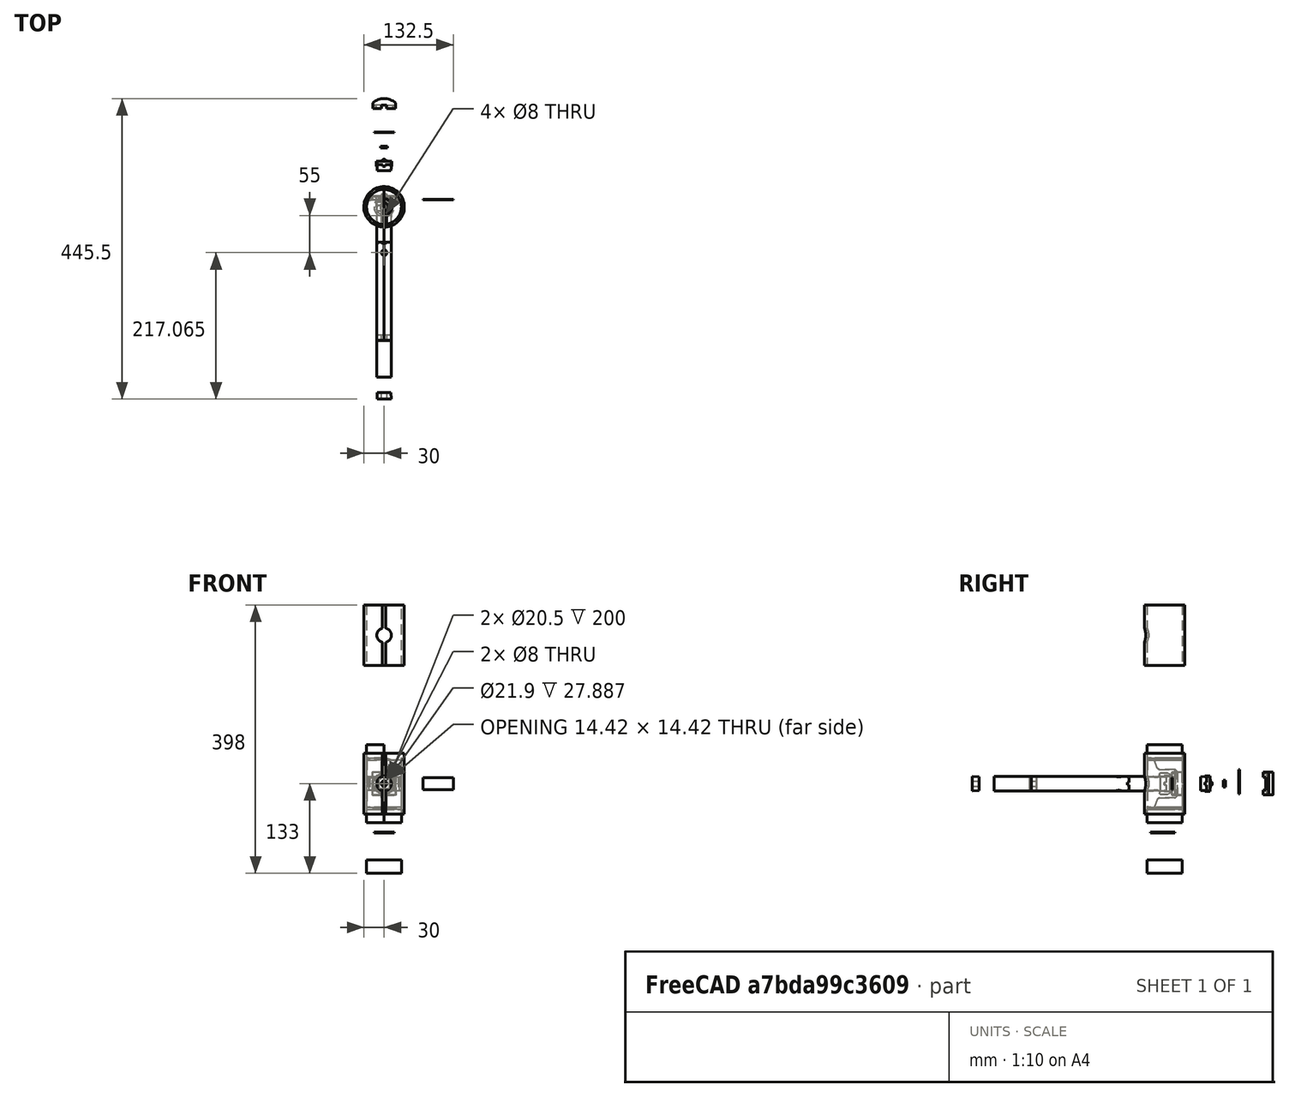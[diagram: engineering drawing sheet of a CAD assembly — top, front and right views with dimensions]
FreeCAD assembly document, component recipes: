
FREECAD ASSEMBLY — COMPONENT RECIPES ("Hammer")

This assembly document has 15 components, labeled P0..P14 below (a component is one placed body or linked part). 15 of them carry a construction recipe — the FreeCAD feature program that regenerates the part from scratch, quoted from this document or its linked companion documents; the rest are supplied as boundary geometry only. No exploded tour is included for this assembly.
NOTE — document 2 of 2 of this assembly tour. The two overview renders and the header above are repeated from document 1; the component sections below continue where the previous document stopped.
COMPONENT P14 — recipe-attached ("PartExploded", modeled in this document).
Construction recipe (the document's own serialized feature program — sketch geometry with constraints, then the solid features built on it; lengths are millimeters unless a unit is written):

FEATURE [Sketcher::SketchObject] Sketch028  label="base001"
  FullyConstrained = true
  MapMode = 5
  Support = -> [XY_Plane016]
  expr: Constraints[1] = <<Properties001>>.Head_ID
  sketch-geometry (1):
    g0: Circle CenterX=0 CenterY=0 CenterZ=0 NormalX=0 NormalY=0 NormalZ=1 AngleXU=0 Radius=25.7
  constraints (2):
    c: Coincident(g0,g-1)
    c: Diameter(g0) = 51.4
FEATURE [PartDesign::Pad] Pad016  label="Base001"
  Direction = (0,0,1)
  Length = 35
  Length2 = 35
  Profile = -> Sketch028
  ReferenceAxis = -> Sketch028 [N_Axis]
  Type = 4
  expr: Length = <<Properties001>>.Insert_Len / 2
  expr: Length2 = <<Properties001>>.Insert_Len / 2
FEATURE [Sketcher::SketchObject] Sketch029  label="sensor_wire_slot001"
  FullyConstrained = true
  MapMode = 5
  Support = -> [XY_Plane016]
  expr: Constraints[11] = <<Properties001>>.Sensor_Wire_Track_Width
  expr: Constraints[1] = Sketch028.Constraints[1]
  sketch-geometry (7):
    g0: Circle CenterX=0 CenterY=0 CenterZ=0 NormalX=0 NormalY=0 NormalZ=1 AngleXU=0 Radius=25.7
    g1: LineSegment StartX=-4 StartY=-25.3868 StartZ=0 EndX=-4 EndY=-14.4568 EndZ=0
    g2: LineSegment StartX=-4 StartY=-14.4568 StartZ=0 EndX=4 EndY=-14.4568 EndZ=0
    g3: LineSegment StartX=4 StartY=-14.4568 StartZ=0 EndX=4 EndY=-25.3868 EndZ=0
    g4: ArcOfCircle CenterX=0 CenterY=0 CenterZ=0 NormalX=0 NormalY=0 NormalZ=1 AngleXU=0 Radius=25.7 StartAngle=4.55611 EndAngle=4.86867
    g5: GeomPoint X=0 Y=-14.4568 Z=0
    g6: Circle CenterX=0 CenterY=0 CenterZ=0 NormalX=0 NormalY=0 NormalZ=1 AngleXU=0 Radius=15
  constraints (17):
    c: Coincident(g0,g-1)
    c: Diameter(g0) = 51.4
    c: Vertical(g1)
    c: Coincident(g2,g1)
    c: Horizontal(g2)
    c: Coincident(g3,g2)
    c: Vertical(g3)
    c: Coincident(g4,g0)
    c: Coincident(g4,g1)
    c: Coincident(g4,g3)
    c: PointOnObject(g3,g0)
    c: DistanceX(g2,g2) = 8
    c: Symmetric(g2,g2,g5)
    c: PointOnObject(g5,g-2)
    c: Coincident(g6,g4)
    c: Diameter(g6) = 30
    c: PointOnObject(g2,g6)
FEATURE [PartDesign::Pocket] Pocket013  label="Sensor_Wire_Slot001"
  BaseFeature = -> Pad016
  Direction = (0,0,-1)
  Length = 35
  Length2 = 35
  Profile = -> Sketch029
  ReferenceAxis = -> Sketch029 [N_Axis]
  Type = 4
  expr: Length = <<Properties001>>.Insert_Len / 2
  expr: Length2 = <<Properties001>>.Insert_Len / 2
FEATURE [Sketcher::SketchObject] Sketch030  label="handle_hole001"
  FullyConstrained = true
  MapMode = 5
  Placement = pos=(0,0,0) rot=(1,0,0;1.5708rad)
  Support = -> [XZ_Plane016]
  expr: Constraints[1] = <<Properties001>>.Handle_OD + <<Properties001>>.Clearance * 2
  sketch-geometry (1):
    g0: Circle CenterX=0 CenterY=0 CenterZ=0 NormalX=0 NormalY=0 NormalZ=1 AngleXU=0 Radius=10.95
  constraints (2):
    c: Coincident(g0,g-1)
    c: Diameter(g0) = 21.9
FEATURE [PartDesign::Pocket] Pocket014  label="Handle_hole001"
  BaseFeature = -> Pocket013
  Direction = (0,1,2e-16)
  Length = 25.7
  Length2 = 25.7
  Profile = -> Sketch030
  ReferenceAxis = -> Sketch030 [N_Axis]
  Type = 4
  expr: Length = <<Properties001>>.Head_ID / 2
  expr: Length2 = <<Properties001>>.Head_ID / 2
FEATURE [Sketcher::SketchObject] Sketch031  label="spring_plate_slot001"
  FullyConstrained = true
  MapMode = 5
  Support = -> [XY_Plane016]
  expr: Constraints[1] = Sketch028.Constraints[1]
  expr: Constraints[3] = <<Properties001>>.Sensor_Diameter + <<Properties001>>.Clearance * 2
  expr: Constraints[7] = <<Properties001>>.Spring_Plate_Len
  sketch-geometry (15):
    g0: Circle CenterX=0 CenterY=0 CenterZ=0 NormalX=0 NormalY=0 NormalZ=1 AngleXU=0 Radius=25.7
    g1: LineSegment StartX=-15.2 StartY=15.4669 StartZ=0 EndX=15.2 EndY=15.4669 EndZ=0
    g2: GeomPoint X=0 Y=15.4669 Z=0
    g3: LineSegment StartX=-23 StartY=11.4669 StartZ=0 EndX=23 EndY=11.4669 EndZ=0
    g4: GeomPoint X=0 Y=11.4669 Z=0
    g5: LineSegment StartX=-15.2 StartY=15.4669 StartZ=0 EndX=-21 EndY=11.4669 EndZ=0
    g6: LineSegment StartX=15.2 StartY=15.4669 StartZ=0 EndX=21 EndY=11.4669 EndZ=0
    g7: LineSegment StartX=21 StartY=11.4669 StartZ=0 EndX=23 EndY=11.4669 EndZ=0
    g8: LineSegment StartX=-21 StartY=11.4669 StartZ=0 EndX=-23 EndY=11.4669 EndZ=0
    g9: ArcOfCircle CenterX=0 CenterY=0 CenterZ=0 NormalX=0 NormalY=0 NormalZ=1 AngleXU=0 Radius=25.7 StartAngle=2.6791 EndAngle=2.80587
    g10: ArcOfCircle CenterX=0 CenterY=0 CenterZ=0 NormalX=0 NormalY=0 NormalZ=1 AngleXU=0 Radius=25.7 StartAngle=0.335723 EndAngle=0.462496
    g11: LineSegment StartX=-11 StartY=10.5 StartZ=0 EndX=-24.2652 EndY=8.46691 EndZ=0
    g12: LineSegment StartX=11 StartY=10.5 StartZ=0 EndX=24.2652 EndY=8.46691 EndZ=0
    g13: LineSegment StartX=11 StartY=10.5 StartZ=0 EndX=-11 EndY=10.5 EndZ=0
    g14: GeomPoint X=0 Y=10.5 Z=0
  constraints (39):
    c: Coincident(g0,g-1)
    c: Diameter(g0) = 51.4
    c: Horizontal(g1)
    c: DistanceX(g1,g1) = 30.4
    c: Symmetric(g1,g1,g2)
    c: PointOnObject(g2,g-2)
    c: Horizontal(g3)
    c: DistanceX(g3,g3) = 46
    c: Symmetric(g3,g3,g4)
    c: PointOnObject(g4,g-2)
    c: Coincident(g5,g1)
    c: PointOnObject(g5,g3)
    c: Coincident(g6,g1)
    c: PointOnObject(g6,g3)
    c: Coincident(g7,g6)
    c: PointOnObject(g7,g0)
    c: Horizontal(g7)
    c: Coincident(g8,g5)
    c: PointOnObject(g8,g0)
    c: Horizontal(g8)
    c: Equal(g8,g7)
    c: PointOnObject(g3,g0)
    c: DistanceY(g6,g1) = 4
    c: DistanceX(g6,g7) = 2
    c: Coincident(g9,g0)
    c: Coincident(g9,g8)
    c: Coincident(g10,g9)
    c: Coincident(g10,g7)
    c: Coincident(g13,g12)
    c: Coincident(g13,g11)
    c: Horizontal(g13)
    c: Coincident(g10,g12)
    c: Coincident(g9,g11)
    c: DistanceX(g12,g6) = 10
    c: Equal(g12,g11)
    c: DistanceY(g10,g7) = 3
    c: Symmetric(g13,g13,g14)
    c: PointOnObject(g14,g-2)
    c: DistanceY(g9,g14) = 10.5
FEATURE [Sketcher::SketchObject] Sketch032  label="top_sensor_hole001"
  FullyConstrained = true
  MapMode = 5
  Placement = pos=(0,0,0) rot=(0.57735,0.57735,0.57735;2.0944rad)
  Support = -> [YZ_Plane016]
  expr: Constraints[20] = <<Properties001>>.Head_ID
  expr: Constraints[7] = <<Properties001>>.Sensor_Diameter + 4
  sketch-geometry (9):
    g0: LineSegment StartX=-25.7 StartY=-17 StartZ=0 EndX=-25.7 EndY=17 EndZ=0
    g1: LineSegment StartX=25.7 StartY=17 StartZ=0 EndX=25.7 EndY=-17 EndZ=0
    g2: LineSegment StartX=25.7 StartY=-17 StartZ=0 EndX=-25.7 EndY=-17 EndZ=0
    g3: GeomPoint X=0 Y=0 Z=0
    g4: LineSegment StartX=10.5 StartY=17 StartZ=0 EndX=25.7 EndY=17 EndZ=0
    g5: LineSegment StartX=25.7 StartY=17 StartZ=0 EndX=25.7 EndY=-17 EndZ=0
    g6: LineSegment StartX=25.7 StartY=-17 StartZ=0 EndX=10.5 EndY=-17 EndZ=0
    g7: LineSegment StartX=10.5 StartY=-17 StartZ=0 EndX=10.5 EndY=17 EndZ=0
    g8: LineSegment StartX=-25.7 StartY=17 StartZ=0 EndX=25.7 EndY=17 EndZ=0
  constraints (23):
    c: Coincident(g1,g2)
    c: Coincident(g2,g0)
    c: Horizontal(g2)
    c: Vertical(g0)
    c: Vertical(g1)
    c: Symmetric(g1,g0,g3)
    c: Coincident(g3,g-1)
    c: DistanceY(g1,g1) = 34
    c: Coincident(g4,g5)
    c: Coincident(g5,g6)
    c: Coincident(g6,g7)
    c: Horizontal(g4)
    c: Horizontal(g6)
    c: Vertical(g5)
    c: Vertical(g7)
    c: PointOnObject(g5,g2)
    c: Coincident(g7,g4)
    c: Coincident(g8,g0)
    c: Coincident(g8,g1)
    c: Horizontal(g8)
    c: DistanceX(g8,g8) = 51.4
    c: Coincident(g4,g1)
    c: DistanceX(g3,g4) = 10.5
FEATURE [PartDesign::Pocket] Pocket015  label="Top_Sensor_Hole001"
  BaseFeature = -> Pocket014
  Direction = (-1,2e-16,-3e-16)
  Length = 17
  Length2 = 17
  Profile = -> Sketch032
  ReferenceAxis = -> Sketch032 [N_Axis]
  Type = 4
  expr: Length = <<Properties001>>.Sensor_Diameter / 2 + 2
  expr: Length2 = <<Properties001>>.Sensor_Diameter / 2 + 2
FEATURE [PartDesign::Chamfer] Chamfer007
  Angle = 70
  Base = -> Pocket015 [Edge30,Edge32]
  BaseFeature = -> Pocket015
  ChamferType = 2
  FlipDirection = false
  Size = 8
  Size2 = 1
  SupportTransform = false
  UseAllEdges = false
FEATURE [PartDesign::Pocket] Pocket016  label="Spring_Plate_Slot001"
  BaseFeature = -> Chamfer007
  Direction = (0,0,-1)
  Length = 10
  Length2 = 10
  Profile = -> Sketch031
  ReferenceAxis = -> Sketch031 [N_Axis]
  Type = 4
FEATURE [PartDesign::Chamfer] Chamfer008
  Angle = 45
  Base = -> Pocket016 [Edge43,Edge46,Edge45,Edge47,Edge44,Edge42]
  BaseFeature = -> Pocket016
  ChamferType = 0
  FlipDirection = false
  Size = 0.5
  Size2 = 1
  SupportTransform = false
  UseAllEdges = false
FEATURE [Sketcher::SketchObject] Sketch033  label="top_sens_base001"
  FullyConstrained = true
  MapMode = 5
  Support = -> [XY_Plane015]
  expr: Constraints[18] = <<Properties001>>.Clearance
  expr: Constraints[1] = <<Properties001>>.Head_ID
  expr: Constraints[3] = 34 - <<Properties001>>.Clearance * 2
  expr: Constraints[6] = 10.5 + <<Properties001>>.Clearance
  sketch-geometry (8):
    g0: Circle CenterX=0 CenterY=0 CenterZ=0 NormalX=0 NormalY=0 NormalZ=1 AngleXU=0 Radius=25.7
    g1: LineSegment StartX=-16.8 StartY=10.7 StartZ=0 EndX=16.8 EndY=10.7 EndZ=0
    g2: GeomPoint X=0 Y=10.7 Z=0
    g3: LineSegment StartX=-16.8 StartY=10.7 StartZ=0 EndX=-16.8 EndY=19.1836 EndZ=0
    g4: LineSegment StartX=16.8 StartY=10.7 StartZ=0 EndX=16.8 EndY=19.1836 EndZ=0
    g5: GeomPoint X=0 Y=25.7 Z=0
    g6: ArcOfCircle CenterX=0 CenterY=0 CenterZ=0 NormalX=0 NormalY=0 NormalZ=1 AngleXU=0 Radius=25.5 StartAngle=0.851542 EndAngle=2.29005
    g7: GeomPoint X=0 Y=25.5 Z=0
  constraints (19):
    c: Coincident(g0,g-1)
    c: Diameter(g0) = 51.4
    c: Horizontal(g1)
    c: DistanceX(g1,g1) = 33.6
    c: Symmetric(g1,g1,g2)
    c: PointOnObject(g2,g-2)
    c: DistanceY(g0,g2) = 10.7
    c: Coincident(g3,g1)
    c: Vertical(g3)
    c: Vertical(g4)
    c: Coincident(g4,g1)
    c: PointOnObject(g5,g0)
    c: PointOnObject(g5,g-2)
    c: Coincident(g6,g0)
    c: Coincident(g6,g3)
    c: Coincident(g6,g4)
    c: PointOnObject(g7,g6)
    c: PointOnObject(g7,g-2)
    c: DistanceY(g7,g5) = 0.2
FEATURE [PartDesign::Pad] Pad017  label="Top_Base001"
  Direction = (0,0,1)
  Length = 16.8
  Length2 = 16.8
  Profile = -> Sketch033
  ReferenceAxis = -> Sketch033 [N_Axis]
  Type = 4
  expr: Length = <<Properties001>>.Sensor_Diameter / 2 + 2 - <<Properties001>>.Clearance
  expr: Length2 = <<Properties001>>.Sensor_Diameter / 2 + 2 - <<Properties001>>.Clearance
FEATURE [Sketcher::SketchObject] Sketch034
  FullyConstrained = true
  MapMode = 5
  Support = -> [XY_Plane015]
  expr: Constraints[1] = Sketch031.Constraints[1]
  expr: Constraints[22] = Sketch031.Constraints[22]
  expr: Constraints[23] = Sketch031.Constraints[23]
  expr: Constraints[33] = Sketch031.Constraints[33]
  expr: Constraints[35] = Sketch031.Constraints[35]
  expr: Constraints[38] = Sketch031.Constraints[38]
  expr: Constraints[3] = Sketch031.Constraints[3]
  expr: Constraints[7] = Sketch031.Constraints[7]
  sketch-geometry (15):
    g0: Circle CenterX=0 CenterY=0 CenterZ=0 NormalX=0 NormalY=0 NormalZ=1 AngleXU=0 Radius=25.7
    g1: LineSegment StartX=-15.2 StartY=15.4669 StartZ=0 EndX=15.2 EndY=15.4669 EndZ=0
    g2: GeomPoint X=0 Y=15.4669 Z=0
    g3: LineSegment StartX=-23 StartY=11.4669 StartZ=0 EndX=23 EndY=11.4669 EndZ=0
    g4: GeomPoint X=0 Y=11.4669 Z=0
    g5: LineSegment StartX=-15.2 StartY=15.4669 StartZ=0 EndX=-21 EndY=11.4669 EndZ=0
    g6: LineSegment StartX=15.2 StartY=15.4669 StartZ=0 EndX=21 EndY=11.4669 EndZ=0
    g7: LineSegment StartX=21 StartY=11.4669 StartZ=0 EndX=23 EndY=11.4669 EndZ=0
    g8: LineSegment StartX=-21 StartY=11.4669 StartZ=0 EndX=-23 EndY=11.4669 EndZ=0
    g9: ArcOfCircle CenterX=0 CenterY=0 CenterZ=0 NormalX=0 NormalY=0 NormalZ=1 AngleXU=0 Radius=25.7 StartAngle=2.6791 EndAngle=2.80587
    g10: ArcOfCircle CenterX=0 CenterY=0 CenterZ=0 NormalX=0 NormalY=0 NormalZ=1 AngleXU=0 Radius=25.7 StartAngle=0.335723 EndAngle=0.462496
    g11: LineSegment StartX=-11 StartY=10.5 StartZ=0 EndX=-24.2652 EndY=8.46691 EndZ=0
    g12: LineSegment StartX=11 StartY=10.5 StartZ=0 EndX=24.2652 EndY=8.46691 EndZ=0
    g13: LineSegment StartX=11 StartY=10.5 StartZ=0 EndX=-11 EndY=10.5 EndZ=0
    g14: GeomPoint X=0 Y=10.5 Z=0
  constraints (40):
    c: Coincident(g0,g-1)
    c: Diameter(g0) = 51.4
    c: Horizontal(g1)
    c: DistanceX(g1,g1) = 30.4
    c: Symmetric(g1,g1,g2)
    c: PointOnObject(g2,g-2)
    c: Horizontal(g3)
    c: DistanceX(g3,g3) = 46
    c: Symmetric(g3,g3,g4)
    c: PointOnObject(g4,g-2)
    c: Coincident(g5,g1)
    c: PointOnObject(g5,g3)
    c: Coincident(g6,g1)
    c: PointOnObject(g6,g3)
    c: Coincident(g7,g6)
    c: PointOnObject(g7,g0)
    c: Horizontal(g7)
    c: Coincident(g8,g5)
    c: PointOnObject(g8,g0)
    c: Horizontal(g8)
    c: Equal(g8,g7)
    c: PointOnObject(g3,g0)
    c: DistanceY(g6,g1) = 4
    c: DistanceX(g6,g7) = 2
    c: Coincident(g9,g0)
    c: Coincident(g9,g8)
    c: Coincident(g10,g9)
    c: Coincident(g10,g7)
    c: Coincident(g13,g12)
    c: Coincident(g13,g11)
    c: Horizontal(g13)
    c: Coincident(g10,g12)
    c: Coincident(g9,g11)
    c: DistanceX(g12,g6) = 10
    c: Equal(g12,g11)
    c: DistanceY(g10,g7) = 3
    c: Symmetric(g13,g13,g14)
    c: PointOnObject(g14,g-2)
    c: DistanceY(g9,g14) = 10.5
    c: DistanceY(g9,g2) = 15.4669
FEATURE [PartDesign::Pocket] Pocket017
  BaseFeature = -> Pad017
  Direction = (0,0,-1)
  Length = 9.5
  Length2 = 9.5
  Profile = -> Sketch034
  ReferenceAxis = -> Sketch034 [N_Axis]
  Type = 4
FEATURE [PartDesign::Chamfer] Chamfer009
  Angle = 45
  Base = -> Pocket017 [Edge22,Edge12]
  BaseFeature = -> Pocket017
  ChamferType = 0
  FlipDirection = false
  Size = 0.3
  Size2 = 1
  SupportTransform = false
  UseAllEdges = false
FEATURE [Sketcher::SketchObject] Sketch035
  FullyConstrained = true
  MapMode = 5
  Placement = pos=(0,0,0) rot=(1,0,0;1.5708rad)
  Support = -> [XZ_Plane015]
  expr: Constraints[11] = <<Properties001>>.Sensor_Wire_Track_Width
  expr: Constraints[1] = <<Properties001>>.Sensor_Diameter + 1
  expr: Constraints[27] = <<Properties001>>.Sensor_Wire_Track_Width
  sketch-geometry (11):
    g0: Circle CenterX=0 CenterY=0 CenterZ=0 NormalX=0 NormalY=0 NormalZ=1 AngleXU=0 Radius=15.5
    g1: LineSegment StartX=-4 StartY=14.975 StartZ=0 EndX=-4 EndY=27.305 EndZ=0
    g2: LineSegment StartX=-4 StartY=27.305 StartZ=0 EndX=4 EndY=27.305 EndZ=0
    g3: LineSegment StartX=4 StartY=27.305 StartZ=0 EndX=4 EndY=14.975 EndZ=0
    g4: GeomPoint X=0 Y=27.305 Z=0
    g5: LineSegment StartX=-4 StartY=-14.975 StartZ=0 EndX=-4 EndY=-27.305 EndZ=0
    g6: LineSegment StartX=-4 StartY=-27.305 StartZ=0 EndX=4 EndY=-27.305 EndZ=0
    g7: LineSegment StartX=4 StartY=-27.305 StartZ=0 EndX=4 EndY=-14.975 EndZ=0
    g8: GeomPoint X=0 Y=-27.305 Z=0
    g9: ArcOfCircle CenterX=0 CenterY=0 CenterZ=0 NormalX=0 NormalY=0 NormalZ=1 AngleXU=0 Radius=15.5 StartAngle=1.83181 EndAngle=4.45137
    g10: ArcOfCircle CenterX=0 CenterY=0 CenterZ=0 NormalX=0 NormalY=0 NormalZ=1 AngleXU=0 Radius=15.5 StartAngle=4.97341 EndAngle=7.59296
  constraints (28):
    c: Coincident(g0,g-1)
    c: Diameter(g0) = 31
    c: PointOnObject(g1,g0)
    c: Vertical(g1)
    c: Coincident(g2,g1)
    c: Horizontal(g2)
    c: Coincident(g3,g2)
    c: PointOnObject(g3,g0)
    c: Vertical(g3)
    c: Symmetric(g2,g2,g4)
    c: PointOnObject(g4,g-2)
    c: DistanceX(g2,g2) = 8
    c: DistanceY(g3,g3) = 12.33
    c: Vertical(g5)
    c: Coincident(g6,g5)
    c: Horizontal(g6)
    c: Coincident(g7,g6)
    c: Vertical(g7)
    c: Symmetric(g6,g6,g8)
    c: PointOnObject(g8,g-2)
    c: Equal(g7,g3)
    c: Coincident(g9,g0)
    c: Coincident(g9,g1)
    c: Coincident(g9,g5)
    c: Coincident(g10,g9)
    c: Coincident(g10,g3)
    c: Coincident(g10,g7)
    c: DistanceX(g6,g6) = 8
FEATURE [PartDesign::Pocket] Pocket018
  BaseFeature = -> Chamfer009
  Direction = (0,1,2e-16)
  Length = 0
  Length2 = 5
  Offset = 0.4
  Profile = -> Sketch035
  ReferenceAxis = -> Sketch035 [N_Axis]
  Type = 3
  UpToFace = -> Chamfer009 [Face11]
FEATURE [PartDesign::Body] Body015  label="TopSensor001"
  Group = -> [Sketch033,Pad017,Sketch034,Pocket017,Chamfer009,Sketch035,Pocket018]
  Origin = -> Origin015
  Placement = pos=(0,135,0) rot=(0,0,1;0rad)
  Tip = -> Pocket018
FEATURE [Sketcher::SketchObject] Sketch036
  FullyConstrained = true
  MapMode = 5
  Placement = pos=(0,0,0) rot=(0.57735,0.57735,0.57735;2.0944rad)
  Support = -> [YZ_Plane016]
  expr: Constraints[16] = <<Properties001>>.Sensor_Diameter + 2
  sketch-geometry (14):
    g0: LineSegment StartX=15.5 StartY=21 StartZ=0 EndX=15.5 EndY=-21 EndZ=0
    g1: LineSegment StartX=15.5 StartY=-21 StartZ=0 EndX=-19.02 EndY=-21 EndZ=0
    g2: LineSegment StartX=-19.02 StartY=-21 StartZ=0 EndX=-19.02 EndY=-16 EndZ=0
    g3: LineSegment StartX=-19.02 StartY=-16 StartZ=0 EndX=10.5 EndY=-16 EndZ=0
    g4: LineSegment StartX=10.5 StartY=-16 StartZ=0 EndX=10.5 EndY=16 EndZ=0
    g5: LineSegment StartX=10.5 StartY=16 StartZ=0 EndX=-19.02 EndY=16 EndZ=0
    g6: LineSegment StartX=-19.02 StartY=16 StartZ=0 EndX=-19.02 EndY=21 EndZ=0
    g7: LineSegment StartX=-19.02 StartY=21 StartZ=0 EndX=15.5 EndY=21 EndZ=0
    g8: GeomPoint X=10.5 Y=0 Z=0
    g9: GeomPoint X=15.5 Y=0 Z=0
    g10: GeomPoint X=15.5 Y=21 Z=0
    g11: GeomPoint X=15.5 Y=-21 Z=0
    g12: GeomPoint X=10.5 Y=16 Z=0
    g13: GeomPoint X=10.5 Y=-16 Z=0
  constraints (30):
    c: Vertical(g0)
    c: Horizontal(g1)
    c: Coincident(g2,g1)
    c: Vertical(g2)
    c: Coincident(g3,g2)
    c: Horizontal(g3)
    c: Vertical(g4)
    c: Horizontal(g5)
    c: Coincident(g6,g5)
    c: Vertical(g6)
    c: Coincident(g7,g6)
    c: Horizontal(g7)
    c: Symmetric(g10,g11,g9)
    c: Symmetric(g13,g12,g8)
    c: PointOnObject(g8,g-1)
    c: PointOnObject(g9,g-1)
    c: DistanceY(g13,g12) = 32
    c: DistanceY(g6,g6) = 5
    c: DistanceX(g8,g9) = 5
    c: DistanceX(g-1,g8) = 10.5
    c: DistanceX(g7,g10) = 34.52
    c: Coincident(g0,g10)
    c: Coincident(g7,g0)
    c: Coincident(g4,g12)
    c: Coincident(g5,g4)
    c: Coincident(g0,g11)
    c: Coincident(g4,g13)
    c: Coincident(g3,g4)
    c: Coincident(g1,g0)
    c: Equal(g3,g5)
FEATURE [PartDesign::Pocket] Pocket019
  BaseFeature = -> Chamfer008
  Direction = (-1,2e-16,-3e-16)
  Length = 4
  Length2 = 4
  Profile = -> Sketch036
  ReferenceAxis = -> Sketch036 [N_Axis]
  Type = 4
  expr: Length = <<Properties001>>.Sensor_Wire_Track_Width / 2
  expr: Length2 = <<Properties001>>.Sensor_Wire_Track_Width / 2
FEATURE [PartDesign::Chamfer] Chamfer010
  Angle = 65
  Base = -> Pocket019 [Edge148,Edge154]
  BaseFeature = -> Pocket019
  ChamferType = 2
  FlipDirection = false
  Size = 3
  Size2 = 1
  SupportTransform = false
  UseAllEdges = false
FEATURE [PartDesign::Chamfer] Chamfer011
  Angle = 45
  Base = -> Chamfer010 [Edge167,Edge85,Edge52,Edge56]
  BaseFeature = -> Chamfer010
  ChamferType = 0
  FlipDirection = false
  Size = 2
  Size2 = 1
  SupportTransform = false
  UseAllEdges = false
FEATURE [PartDesign::Chamfer] Chamfer012
  Angle = 45
  Base = -> Chamfer011 [Edge169,Edge38]
  BaseFeature = -> Chamfer011
  ChamferType = 1
  FlipDirection = false
  Size = 4
  Size2 = 3.999
  SupportTransform = false
  UseAllEdges = false
FEATURE [PartDesign::AdditiveCone] Cone002
  Angle = 360
  AttacherType = Attacher::AttachEngine3D
  BaseFeature = -> Chamfer012
  Height = 1.5
  MapMode = 5
  Placement = pos=(0,0,35) rot=(0,0,1;0rad)
  Radius1 = 12
  Radius2 = 6
  Support = -> [Chamfer012]
FEATURE [PartDesign::AdditiveCone] Cone003
  Angle = 360
  AttacherType = Attacher::AttachEngine3D
  BaseFeature = -> Cone002
  Height = 1.5
  MapMode = 5
  Placement = pos=(0,0,-35) rot=(1,0,0;3.14159rad)
  Radius1 = 12
  Radius2 = 6
  Support = -> [Cone002]
FEATURE [Sketcher::SketchObject] Sketch037
  FullyConstrained = true
  MapMode = 5
  Support = -> [XY_Plane017]
  sketch-geometry (2):
    g0: Circle CenterX=0 CenterY=0 CenterZ=0 NormalX=0 NormalY=0 NormalZ=1 AngleXU=0 Radius=26
    g1: Circle CenterX=0 CenterY=0 CenterZ=0 NormalX=0 NormalY=0 NormalZ=1 AngleXU=0 Radius=30
  constraints (4):
    c: Coincident(g0,g-1)
    c: Coincident(g1,g0)
    c: Diameter(g0) = 52
    c: Diameter(g1) = 60
FEATURE [PartDesign::Pad] Pad018
  Direction = (0,0,1)
  Length = 45
  Length2 = 45
  Profile = -> Sketch037
  ReferenceAxis = -> Sketch037 [N_Axis]
  Type = 4
FEATURE [Sketcher::SketchObject] Sketch038
  FullyConstrained = true
  MapMode = 5
  Placement = pos=(0,0,0) rot=(1,0,0;1.5708rad)
  Support = -> [XZ_Plane017]
  expr: Constraints[1] = <<Properties001>>.Handle_OD
  sketch-geometry (1):
    g0: Circle CenterX=0 CenterY=0 CenterZ=0 NormalX=0 NormalY=0 NormalZ=1 AngleXU=0 Radius=10.75
  constraints (2):
    c: Coincident(g0,g-1)
    c: Diameter(g0) = 21.5
FEATURE [PartDesign::Pocket] Pocket020
  BaseFeature = -> Pad018
  Direction = (0,1,2e-16)
  Length = 5
  Length2 = 5
  Profile = -> Sketch038
  ReferenceAxis = -> Sketch038 [N_Axis]
  Reversed = true
  Type = 1
FEATURE [Sketcher::SketchObject] Sketch039
  FullyConstrained = true
  MapMode = 5
  Placement = pos=(0,0,0) rot=(1,0,0;1.5708rad)
  Support = -> [XZ_Plane018]
  expr: Constraints[3] = <<Properties001>>.Handle_ID
  sketch-geometry (2):
    g0: Circle CenterX=0 CenterY=0 CenterZ=0 NormalX=0 NormalY=0 NormalZ=1 AngleXU=0 Radius=10.625
    g1: Circle CenterX=0 CenterY=0 CenterZ=0 NormalX=0 NormalY=0 NormalZ=1 AngleXU=0 Radius=10.25
  constraints (4):
    c: Coincident(g0,g-1)
    c: Diameter(g0) = 21.25
    c: Coincident(g1,g0)
    c: Diameter(g1) = 20.5
FEATURE [PartDesign::Pad] Pad019
  Direction = (0,-1,-2e-16)
  Length = 200
  Length2 = 10
  Placement = pos=(0,0,0) rot=(1,0,0;1.5708rad)
  Profile = -> Sketch039
  ReferenceAxis = -> Sketch039 [N_Axis]
  Type = 0
FEATURE [Sketcher::SketchObject] Sketch040
  FullyConstrained = true
  MapMode = 5
  Support = -> [XY_Plane019]
  sketch-geometry (5):
    g0: ArcOfCircle CenterX=0 CenterY=0 CenterZ=0 NormalX=0 NormalY=0 NormalZ=1 AngleXU=0 Radius=15 StartAngle=4.90695 EndAngle=10.801
    g1: LineSegment StartX=2.9 StartY=-14.717 StartZ=0 EndX=2.9 EndY=-20.717 EndZ=0
    g2: LineSegment StartX=2.9 StartY=-20.717 StartZ=0 EndX=-2.9 EndY=-20.717 EndZ=0
    g3: LineSegment StartX=-2.9 StartY=-20.717 StartZ=0 EndX=-2.9 EndY=-14.717 EndZ=0
    g4: LineSegment StartX=2.9 StartY=-14.717 StartZ=0 EndX=-2.9 EndY=-14.717 EndZ=0
  constraints (14):
    c: Coincident(g0,g-1)
    c: Radius(g0) = 15
    c: Coincident(g1,g0)
    c: Vertical(g1)
    c: Coincident(g2,g1)
    c: Horizontal(g2)
    c: Coincident(g3,g2)
    c: Coincident(g3,g0)
    c: Vertical(g3)
    c: DistanceX(g2,g2) = 5.8
    c: Coincident(g4,g0)
    c: Coincident(g4,g0)
    c: Horizontal(g4)
    c: DistanceY(g1,g1) = 6
FEATURE [PartDesign::Pad] Pad020
  Direction = (0,0,1)
  Length = 1
  Length2 = 10
  Profile = -> Sketch040
  ReferenceAxis = -> Sketch040 [N_Axis]
  Type = 0
FEATURE [PartDesign::Body] Body018  label="Sensor004"
  Group = -> [Sketch040,Pad020]
  Origin = -> Origin019
  Placement = pos=(0,0,72) rot=(0,0,1;0rad)
  Tip = -> Pad020
FEATURE [PartDesign::FeatureBase] Clone003
  BaseFeature = -> Body018
FEATURE [PartDesign::Body] Body019  label="Sensor005"
  Group = -> [Clone003]
  Origin = -> Origin020
  Placement = pos=(0,0,-72) rot=(0,1,0;3.14159rad)
  Tip = -> Clone003
FEATURE [PartDesign::FeatureBase] Clone004
  BaseFeature = -> Body018
FEATURE [PartDesign::Body] Body020  label="Sensor006"
  Group = -> [Clone004]
  Origin = -> Origin021
  Placement = pos=(0,111,1.7e-14) rot=(0,0.707107,-0.707107;3.14159rad)
  Tip = -> Clone004
FEATURE [Sketcher::SketchObject] Sketch041
  FullyConstrained = true
  MapMode = 5
  Support = -> [XY_Plane022]
  sketch-geometry (1):
    g0: Circle CenterX=0 CenterY=0 CenterZ=0 NormalX=0 NormalY=0 NormalZ=1 AngleXU=0 Radius=26
  constraints (2):
    c: Coincident(g0,g-1)
    c: Diameter(g0) = 52
FEATURE [PartDesign::Pad] Pad021
  Direction = (0,0,1)
  Length = 20
  Length2 = 10
  Profile = -> Sketch041
  ReferenceAxis = -> Sketch041 [N_Axis]
  Type = 0
FEATURE [PartDesign::Body] Body021  label="Foam003"
  Group = -> [Sketch041,Pad021]
  Origin = -> Origin022
  Placement = pos=(0,0,108) rot=(0,0,1;0rad)
  Tip = -> Pad021
FEATURE [PartDesign::FeatureBase] Clone005
  BaseFeature = -> Body021
  Placement = pos=(0,0,38) rot=(0,0,1;0rad)
FEATURE [PartDesign::Body] Body022  label="Foam004"
  Group = -> [Clone005]
  Origin = -> Origin023
  Placement = pos=(0,0,-75) rot=(1,0,0;3.14159rad)
  Tip = -> Clone005
FEATURE [Sketcher::SketchObject] Sketch042
  FullyConstrained = true
  MapMode = 5
  Support = -> [XY_Plane024]
  sketch-geometry (5):
    g0: LineSegment StartX=-22.5 StartY=-0.4 StartZ=0 EndX=-22.5 EndY=0.4 EndZ=0
    g1: LineSegment StartX=-22.5 StartY=0.4 StartZ=0 EndX=22.5 EndY=0.4 EndZ=0
    g2: LineSegment StartX=22.5 StartY=0.4 StartZ=0 EndX=22.5 EndY=-0.4 EndZ=0
    g3: LineSegment StartX=22.5 StartY=-0.4 StartZ=0 EndX=-22.5 EndY=-0.4 EndZ=0
    g4: GeomPoint X=0 Y=0 Z=0
  constraints (12):
    c: Coincident(g0,g1)
    c: Coincident(g1,g2)
    c: Coincident(g2,g3)
    c: Coincident(g3,g0)
    c: Horizontal(g1)
    c: Horizontal(g3)
    c: Vertical(g0)
    c: Vertical(g2)
    c: Symmetric(g1,g0,g4)
    c: Coincident(g4,g-1)
    c: DistanceX(g1,g1) = 45
    c: DistanceY(g2,g2) = 0.8
FEATURE [PartDesign::Pad] Pad022
  Direction = (0,0,1)
  Length = 9
  Length2 = 9
  Profile = -> Sketch042
  ReferenceAxis = -> Sketch042 [N_Axis]
  Type = 4
FEATURE [PartDesign::Body] Body023  label="ShimStock001"
  Group = -> [Sketch042,Pad022]
  Origin = -> Origin024
  Placement = pos=(80,11,0) rot=(0,0,1;0rad)
  Tip = -> Pad022
FEATURE [Sketcher::SketchObject] Sketch043
  FullyConstrained = true
  MapMode = 5
  Placement = pos=(0,0,0) rot=(1,0,0;1.5708rad)
  Support = -> [XZ_Plane025]
  sketch-geometry (1):
    g0: Circle CenterX=0 CenterY=0 CenterZ=0 NormalX=0 NormalY=0 NormalZ=1 AngleXU=0 Radius=5
  constraints (2):
    c: Coincident(g0,g-1)
    c: Diameter(g0) = 10
FEATURE [PartDesign::Pad] Pad023
  Direction = (0,-1,-2e-16)
  Length = 3
  Length2 = 10
  Placement = pos=(0,0,0) rot=(1,0,0;1.5708rad)
  Profile = -> Sketch043
  ReferenceAxis = -> Sketch043 [N_Axis]
  Type = 0
FEATURE [PartDesign::Body] Body024  label="TopFoam001"
  Group = -> [Sketch043,Pad023]
  Origin = -> Origin025
  Placement = pos=(0,90,0) rot=(0,0,1;0rad)
  Tip = -> Pad023
FEATURE [Sketcher::SketchObject] Sketch044
  FullyConstrained = false
  MapMode = 5
  Support = -> [XY_Plane018]
  sketch-geometry (1):
    g0: Circle CenterX=0 CenterY=-15.4348 CenterZ=0 NormalX=0 NormalY=0 NormalZ=1 AngleXU=0 Radius=4
  constraints (2):
    c: PointOnObject(g0,g-2)
    c: Diameter(g0) = 8
FEATURE [PartDesign::Pocket] Pocket021
  BaseFeature = -> Pad019
  Direction = (0,0,-1)
  Length = 50
  Length2 = 50
  Placement = pos=(0,0,0) rot=(1,0,0;1.5708rad)
  Profile = -> Sketch044
  ReferenceAxis = -> Sketch044 [N_Axis]
  Type = 4
FEATURE [Sketcher::SketchObject] Sketch045
  FullyConstrained = true
  MapMode = 5
  Placement = pos=(0,0,0) rot=(1,0,0;1.5708rad)
  Support = -> [XZ_Plane018]
  sketch-geometry (17):
    g0: LineSegment StartX=12 StartY=-2 StartZ=0 EndX=12 EndY=2 EndZ=0
    g1: LineSegment StartX=12 StartY=2 StartZ=0 EndX=2 EndY=2 EndZ=0
    g2: LineSegment StartX=2 StartY=2 StartZ=0 EndX=2 EndY=12 EndZ=0
    g3: LineSegment StartX=2 StartY=12 StartZ=0 EndX=-2 EndY=12 EndZ=0
    g4: LineSegment StartX=-2 StartY=12 StartZ=0 EndX=-2 EndY=2 EndZ=0
    g5: LineSegment StartX=-2 StartY=2 StartZ=0 EndX=-12 EndY=2 EndZ=0
    g6: LineSegment StartX=-12 StartY=2 StartZ=0 EndX=-12 EndY=-2 EndZ=0
    g7: LineSegment StartX=-12 StartY=-2 StartZ=0 EndX=-2 EndY=-2 EndZ=0
    g8: LineSegment StartX=-2 StartY=-2 StartZ=0 EndX=-2 EndY=-12 EndZ=0
    g9: LineSegment StartX=-2 StartY=-12 StartZ=0 EndX=2 EndY=-12 EndZ=0
    g10: LineSegment StartX=2 StartY=-12 StartZ=0 EndX=2 EndY=-2 EndZ=0
    g11: LineSegment StartX=2 StartY=-2 StartZ=0 EndX=12 EndY=-2 EndZ=0
    g12: LineSegment StartX=-2 StartY=-2 StartZ=0 EndX=-2 EndY=2 EndZ=0
    g13: LineSegment StartX=-2 StartY=2 StartZ=0 EndX=2 EndY=2 EndZ=0
    g14: LineSegment StartX=2 StartY=2 StartZ=0 EndX=2 EndY=-2 EndZ=0
    g15: LineSegment StartX=2 StartY=-2 StartZ=0 EndX=-2 EndY=-2 EndZ=0
    g16: GeomPoint X=0 Y=0 Z=0
  constraints (46):
    c: Vertical(g0)
    c: Coincident(g1,g0)
    c: Horizontal(g1)
    c: Coincident(g2,g1)
    c: Vertical(g2)
    c: Coincident(g3,g2)
    c: Horizontal(g3)
    c: Coincident(g4,g3)
    c: Vertical(g4)
    c: Coincident(g5,g4)
    c: Horizontal(g5)
    c: Coincident(g6,g5)
    c: Vertical(g6)
    c: Horizontal(g7)
    c: Coincident(g8,g7)
    c: Vertical(g8)
    c: Horizontal(g9)
    c: Coincident(g10,g9)
    c: Vertical(g10)
    c: Coincident(g11,g10)
    c: Coincident(g11,g0)
    c: Horizontal(g11)
    c: Equal(g0,g3)
    c: Equal(g3,g6)
    c: Equal(g6,g9)
    c: Coincident(g6,g7)
    c: Coincident(g9,g8)
    c: Equal(g11,g7)
    c: Equal(g11,g1)
    c: Equal(g2,g4)
    c: Equal(g5,g10)
    c: Coincident(g12,g13)
    c: Coincident(g13,g14)
    c: Coincident(g14,g15)
    c: Coincident(g15,g12)
    c: Horizontal(g13)
    c: Horizontal(g15)
    c: Vertical(g12)
    c: Vertical(g14)
    c: Symmetric(g13,g12,g16)
    c: Coincident(g16,g-1)
    c: Coincident(g13,g1)
    c: Coincident(g7,g12)
    c: DistanceX(g13,g13) = 4
    c: DistanceY(g2,g2) = 10
    c: Equal(g10,g2)
FEATURE [PartDesign::Pocket] Pocket022
  BaseFeature = -> Pocket021
  Direction = (0,1,2e-16)
  Length = 3
  Length2 = 5
  Placement = pos=(0,0,0) rot=(1,0,0;1.5708rad)
  Profile = -> Sketch045
  ReferenceAxis = -> Sketch045 [N_Axis]
  Reversed = true
  Type = 0
FEATURE [PartDesign::Body] Body017  label="MetalHandle001"
  Group = -> [Sketch039,Pad019,Sketch044,Pocket021,Sketch045,Pocket022]
  Origin = -> Origin018
  Placement = pos=(0,-52.5,0) rot=(0,0,1;0rad)
  Tip = -> Pocket022
FEATURE [Sketcher::SketchObject] Sketch046
  FullyConstrained = true
  MapMode = 5
  Placement = pos=(0,0,0) rot=(1,0,0;1.5708rad)
  Support = -> [XZ_Plane026]
  expr: Constraints[43] = Sketch045.Constraints[43]
  expr: Constraints[44] = Sketch045.Constraints[44]
  expr: Constraints[77] = <<Properties001>>.Clearance
  expr: Constraints[78] = <<Properties001>>.Clearance
  expr: Constraints[79] = <<Properties001>>.Clearance
  expr: Constraints[81] = (<<Properties001>>.Handle_OD + 2) / 2 - <<Properties001>>.Clearance
  sketch-geometry (29):
    g0: LineSegment StartX=12 StartY=-2 StartZ=0 EndX=12 EndY=2 EndZ=0
    g1: LineSegment StartX=12 StartY=2 StartZ=0 EndX=2 EndY=2 EndZ=0
    g2: LineSegment StartX=2 StartY=2 StartZ=0 EndX=2 EndY=12 EndZ=0
    g3: LineSegment StartX=2 StartY=12 StartZ=0 EndX=-2 EndY=12 EndZ=0
    g4: LineSegment StartX=-2 StartY=12 StartZ=0 EndX=-2 EndY=2 EndZ=0
    g5: LineSegment StartX=-2 StartY=2 StartZ=0 EndX=-12 EndY=2 EndZ=0
    g6: LineSegment StartX=-12 StartY=2 StartZ=0 EndX=-12 EndY=-2 EndZ=0
    g7: LineSegment StartX=-12 StartY=-2 StartZ=0 EndX=-2 EndY=-2 EndZ=0
    g8: LineSegment StartX=-2 StartY=-2 StartZ=0 EndX=-2 EndY=-12 EndZ=0
    g9: LineSegment StartX=-2 StartY=-12 StartZ=0 EndX=2 EndY=-12 EndZ=0
    g10: LineSegment StartX=2 StartY=-12 StartZ=0 EndX=2 EndY=-2 EndZ=0
    g11: LineSegment StartX=2 StartY=-2 StartZ=0 EndX=12 EndY=-2 EndZ=0
    g12: LineSegment StartX=-2 StartY=-2 StartZ=0 EndX=-2 EndY=2 EndZ=0
    g13: LineSegment StartX=-2 StartY=2 StartZ=0 EndX=2 EndY=2 EndZ=0
    g14: LineSegment StartX=2 StartY=2 StartZ=0 EndX=2 EndY=-2 EndZ=0
    g15: LineSegment StartX=2 StartY=-2 StartZ=0 EndX=-2 EndY=-2 EndZ=0
    g16: GeomPoint X=0 Y=0 Z=0
    g17: LineSegment StartX=-1.8 StartY=11.55 StartZ=0 EndX=-1.8 EndY=1.8 EndZ=0
    g18: LineSegment StartX=-1.8 StartY=1.8 StartZ=0 EndX=-11.55 EndY=1.8 EndZ=0
    g19: LineSegment StartX=-11.55 StartY=1.8 StartZ=0 EndX=-11.55 EndY=-1.8 EndZ=0
    g20: LineSegment StartX=-11.55 StartY=-1.8 StartZ=0 EndX=-1.8 EndY=-1.8 EndZ=0
    g21: LineSegment StartX=-1.8 StartY=-1.8 StartZ=0 EndX=-1.8 EndY=-11.55 EndZ=0
    g22: LineSegment StartX=-1.8 StartY=-11.55 StartZ=0 EndX=1.8 EndY=-11.55 EndZ=0
    g23: LineSegment StartX=1.8 StartY=-11.55 StartZ=0 EndX=1.8 EndY=-1.8 EndZ=0
    g24: LineSegment StartX=1.8 StartY=-1.8 StartZ=0 EndX=11.55 EndY=-1.8 EndZ=0
    g25: LineSegment StartX=11.55 StartY=-1.8 StartZ=0 EndX=11.55 EndY=1.8 EndZ=0
    g26: LineSegment StartX=11.55 StartY=1.8 StartZ=0 EndX=1.8 EndY=1.8 EndZ=0
    g27: LineSegment StartX=1.8 StartY=1.8 StartZ=0 EndX=1.8 EndY=11.55 EndZ=0
    g28: LineSegment StartX=1.8 StartY=11.55 StartZ=0 EndX=-1.8 EndY=11.55 EndZ=0
  constraints (82):
    c: Vertical(g0)
    c: Coincident(g1,g0)
    c: Horizontal(g1)
    c: Coincident(g2,g1)
    c: Vertical(g2)
    c: Coincident(g3,g2)
    c: Horizontal(g3)
    c: Coincident(g4,g3)
    c: Vertical(g4)
    c: Coincident(g5,g4)
    c: Horizontal(g5)
    c: Coincident(g6,g5)
    c: Vertical(g6)
    c: Horizontal(g7)
    c: Coincident(g8,g7)
    c: Vertical(g8)
    c: Horizontal(g9)
    c: Coincident(g10,g9)
    c: Vertical(g10)
    c: Coincident(g11,g10)
    c: Coincident(g11,g0)
    c: Horizontal(g11)
    c: Equal(g0,g3)
    c: Equal(g3,g6)
    c: Equal(g6,g9)
    c: Coincident(g6,g7)
    c: Coincident(g9,g8)
    c: Equal(g11,g7)
    c: Equal(g11,g1)
    c: Equal(g2,g4)
    c: Equal(g5,g10)
    c: Coincident(g12,g13)
    c: Coincident(g13,g14)
    c: Coincident(g14,g15)
    c: Coincident(g15,g12)
    c: Horizontal(g13)
    c: Horizontal(g15)
    c: Vertical(g12)
    c: Vertical(g14)
    c: Symmetric(g13,g12,g16)
    c: Coincident(g16,g-1)
    c: Coincident(g13,g1)
    c: Coincident(g7,g12)
    c: DistanceX(g13,g13) = 4
    c: DistanceY(g2,g2) = 10
    c: Equal(g10,g2)
    c: Vertical(g17)
    c: Coincident(g18,g17)
    c: Horizontal(g18)
    c: Coincident(g19,g18)
    c: Vertical(g19)
    c: Coincident(g20,g19)
    c: Horizontal(g20)
    c: Coincident(g21,g20)
    c: Vertical(g21)
    c: Coincident(g22,g21)
    c: Horizontal(g22)
    c: Coincident(g23,g22)
    c: Vertical(g23)
    c: Coincident(g24,g23)
    c: Horizontal(g24)
    c: Coincident(g25,g24)
    c: Vertical(g25)
    c: Coincident(g26,g25)
    c: Horizontal(g26)
    c: Coincident(g27,g26)
    c: Vertical(g27)
    c: Coincident(g28,g27)
    c: Coincident(g28,g17)
    c: Horizontal(g28)
    c: Equal(g26,g18)
    c: Equal(g27,g17)
    c: Equal(g26,g24)
    c: Equal(g20,g24)
    c: Equal(g21,g23)
    c: Equal(g23,g27)
    c: Equal(g22,g25)
    c: DistanceX(g26,g1) = 0.2
    c: DistanceY(g26,g1) = 0.2
    c: DistanceY(g0,g24) = 0.2
    c: Equal(g23,g24)
    c: DistanceX(g16,g25) = 11.55
FEATURE [PartDesign::Pad] Pad024
  Direction = (0,-1,2e-16)
  Length = 2.8
  Length2 = 10
  Placement = pos=(0,0,0) rot=(1,0,0;1.5708rad)
  Profile = -> Sketch046
  ReferenceAxis = -> Sketch046 [N_Axis]
  Type = 0
FEATURE [Sketcher::SketchObject] Sketch047
  FullyConstrained = true
  MapMode = 5
  Placement = pos=(0,0,0) rot=(1,0,0;1.5708rad)
  Support = -> [XZ_Plane026]
  expr: Constraints[53] = Sketch046.Constraints[43]
  expr: Constraints[54] = Sketch046.Constraints[44]
  expr: Constraints[87] = Sketch046.Constraints[77]
  expr: Constraints[88] = Sketch046.Constraints[78]
  expr: Constraints[89] = Sketch046.Constraints[79]
  expr: Constraints[91] = Sketch046.Constraints[81]
  sketch-geometry (34):
    g0: LineSegment StartX=11.55 StartY=11.55 StartZ=0 EndX=11.55 EndY=-11.55 EndZ=0
    g1: LineSegment StartX=11.55 StartY=-11.55 StartZ=0 EndX=-11.55 EndY=-11.55 EndZ=0
    g2: LineSegment StartX=-11.55 StartY=-11.55 StartZ=0 EndX=-11.55 EndY=11.55 EndZ=0
    g3: LineSegment StartX=-11.55 StartY=11.55 StartZ=0 EndX=11.55 EndY=11.55 EndZ=0
    g4: GeomPoint X=0 Y=0 Z=0
    g5: LineSegment StartX=12 StartY=-2 StartZ=0 EndX=12 EndY=2 EndZ=0
    g6: LineSegment StartX=12 StartY=2 StartZ=0 EndX=2 EndY=2 EndZ=0
    g7: LineSegment StartX=2 StartY=2 StartZ=0 EndX=2 EndY=12 EndZ=0
    g8: LineSegment StartX=2 StartY=12 StartZ=0 EndX=-2 EndY=12 EndZ=0
    g9: LineSegment StartX=-2 StartY=12 StartZ=0 EndX=-2 EndY=2 EndZ=0
    g10: LineSegment StartX=-2 StartY=2 StartZ=0 EndX=-12 EndY=2 EndZ=0
    g11: LineSegment StartX=-12 StartY=2 StartZ=0 EndX=-12 EndY=-2 EndZ=0
    g12: LineSegment StartX=-12 StartY=-2 StartZ=0 EndX=-2 EndY=-2 EndZ=0
    g13: LineSegment StartX=-2 StartY=-2 StartZ=0 EndX=-2 EndY=-12 EndZ=0
    g14: LineSegment StartX=-2 StartY=-12 StartZ=0 EndX=2 EndY=-12 EndZ=0
    g15: LineSegment StartX=2 StartY=-12 StartZ=0 EndX=2 EndY=-2 EndZ=0
    g16: LineSegment StartX=2 StartY=-2 StartZ=0 EndX=12 EndY=-2 EndZ=0
    g17: LineSegment StartX=-2 StartY=-2 StartZ=0 EndX=-2 EndY=2 EndZ=0
    g18: LineSegment StartX=-2 StartY=2 StartZ=0 EndX=2 EndY=2 EndZ=0
    g19: LineSegment StartX=2 StartY=2 StartZ=0 EndX=2 EndY=-2 EndZ=0
    g20: LineSegment StartX=2 StartY=-2 StartZ=0 EndX=-2 EndY=-2 EndZ=0
    g21: GeomPoint X=0 Y=0 Z=0
    g22: LineSegment StartX=-1.8 StartY=11.55 StartZ=0 EndX=-1.8 EndY=1.8 EndZ=0
    g23: LineSegment StartX=-1.8 StartY=1.8 StartZ=0 EndX=-11.55 EndY=1.8 EndZ=0
    g24: LineSegment StartX=-11.55 StartY=1.8 StartZ=0 EndX=-11.55 EndY=-1.8 EndZ=0
    g25: LineSegment StartX=-11.55 StartY=-1.8 StartZ=0 EndX=-1.8 EndY=-1.8 EndZ=0
    g26: LineSegment StartX=-1.8 StartY=-1.8 StartZ=0 EndX=-1.8 EndY=-11.55 EndZ=0
    g27: LineSegment StartX=-1.8 StartY=-11.55 StartZ=0 EndX=1.8 EndY=-11.55 EndZ=0
    g28: LineSegment StartX=1.8 StartY=-11.55 StartZ=0 EndX=1.8 EndY=-1.8 EndZ=0
    g29: LineSegment StartX=1.8 StartY=-1.8 StartZ=0 EndX=11.55 EndY=-1.8 EndZ=0
    g30: LineSegment StartX=11.55 StartY=-1.8 StartZ=0 EndX=11.55 EndY=1.8 EndZ=0
    g31: LineSegment StartX=11.55 StartY=1.8 StartZ=0 EndX=1.8 EndY=1.8 EndZ=0
    g32: LineSegment StartX=1.8 StartY=1.8 StartZ=0 EndX=1.8 EndY=11.55 EndZ=0
    g33: LineSegment StartX=1.8 StartY=11.55 StartZ=0 EndX=-1.8 EndY=11.55 EndZ=0
  constraints (94):
    c: Coincident(g0,g1)
    c: Coincident(g1,g2)
    c: Coincident(g2,g3)
    c: Coincident(g3,g0)
    c: Horizontal(g1)
    c: Horizontal(g3)
    c: Vertical(g0)
    c: Vertical(g2)
    c: Symmetric(g1,g0,g4)
    c: Coincident(g4,g-1)
    c: Vertical(g5)
    c: Coincident(g6,g5)
    c: Horizontal(g6)
    c: Coincident(g7,g6)
    c: Vertical(g7)
    c: Coincident(g8,g7)
    c: Horizontal(g8)
    c: Coincident(g9,g8)
    c: Vertical(g9)
    c: Coincident(g10,g9)
    c: Horizontal(g10)
    c: Coincident(g11,g10)
    c: Vertical(g11)
    c: Horizontal(g12)
    c: Coincident(g13,g12)
    c: Vertical(g13)
    c: Horizontal(g14)
    c: Coincident(g15,g14)
    c: Vertical(g15)
    c: Coincident(g16,g15)
    c: Coincident(g16,g5)
    c: Horizontal(g16)
    c: Equal(g5,g8)
    c: Equal(g8,g11)
    c: Equal(g11,g14)
    c: Coincident(g11,g12)
    c: Coincident(g14,g13)
    c: Equal(g16,g12)
    c: Equal(g16,g6)
    c: Equal(g7,g9)
    c: Equal(g10,g15)
    c: Coincident(g17,g18)
    c: Coincident(g18,g19)
    c: Coincident(g19,g20)
    c: Coincident(g20,g17)
    c: Horizontal(g18)
    c: Horizontal(g20)
    c: Vertical(g17)
    c: Vertical(g19)
    c: Symmetric(g18,g17,g21)
    c: Coincident(g21,g-1)
    c: Coincident(g18,g6)
    c: Coincident(g12,g17)
    c: DistanceX(g18,g18) = 4
    c: DistanceY(g7,g7) = 10
    c: Equal(g15,g7)
    c: Vertical(g22)
    c: Coincident(g23,g22)
    c: Horizontal(g23)
    c: Coincident(g24,g23)
    c: Vertical(g24)
    c: Coincident(g25,g24)
    c: Horizontal(g25)
    c: Coincident(g26,g25)
    c: Vertical(g26)
    c: Coincident(g27,g26)
    c: Horizontal(g27)
    c: Coincident(g28,g27)
    c: Vertical(g28)
    c: Coincident(g29,g28)
    c: Horizontal(g29)
    c: Coincident(g30,g29)
    c: Vertical(g30)
    c: Coincident(g31,g30)
    c: Horizontal(g31)
    c: Coincident(g32,g31)
    c: Vertical(g32)
    c: Coincident(g33,g32)
    c: Coincident(g33,g22)
    c: Horizontal(g33)
    c: Equal(g31,g23)
    c: Equal(g32,g22)
    c: Equal(g31,g29)
    c: Equal(g25,g29)
    c: Equal(g26,g28)
    c: Equal(g28,g32)
    c: Equal(g27,g30)
    c: DistanceX(g31,g6) = 0.2
    c: DistanceY(g31,g6) = 0.2
    c: DistanceY(g5,g29) = 0.2
    c: Equal(g28,g29)
    c: DistanceX(g21,g30) = 11.55
    c: PointOnObject(g22,g3)
    c: PointOnObject(g23,g2)
FEATURE [PartDesign::Pad] Pad025
  BaseFeature = -> Pad024
  Direction = (0,-1,2e-16)
  Length = 5
  Length2 = 10
  Placement = pos=(0,0,0) rot=(1,0,0;1.5708rad)
  Profile = -> Sketch047
  ReferenceAxis = -> Sketch047 [N_Axis]
  Reversed = true
  Type = 0
FEATURE [Sketcher::SketchObject] Sketch048
  ExternalGeometry = -> [Cone003]
  FullyConstrained = true
  MapMode = 5
  Placement = pos=(2.3e-15,10.5,-35) rot=(-1,0,0;1.5708rad)
  Support = -> [Cone003]
  expr: Constraints[11] = <<Properties001>>.Handle_OD + 2
  sketch-geometry (5):
    g0: LineSegment StartX=-11.75 StartY=-46.75 StartZ=0 EndX=-11.75 EndY=-23.25 EndZ=0
    g1: LineSegment StartX=-11.75 StartY=-23.25 StartZ=0 EndX=11.75 EndY=-23.25 EndZ=0
    g2: LineSegment StartX=11.75 StartY=-23.25 StartZ=0 EndX=11.75 EndY=-46.75 EndZ=0
    g3: LineSegment StartX=11.75 StartY=-46.75 StartZ=0 EndX=-11.75 EndY=-46.75 EndZ=0
    g4: GeomPoint X=-2.3e-15 Y=-35 Z=0
  constraints (12):
    c: Coincident(g0,g1)
    c: Coincident(g1,g2)
    c: Coincident(g2,g3)
    c: Coincident(g3,g0)
    c: Horizontal(g1)
    c: Horizontal(g3)
    c: Vertical(g0)
    c: Vertical(g2)
    c: Symmetric(g1,g0,g4)
    c: Coincident(g4,g-3)
    c: Equal(g2,g1)
    c: DistanceX(g1,g1) = 23.5
FEATURE [PartDesign::Pocket] Pocket023
  BaseFeature = -> Cone003
  Direction = (-2e-16,-1,2e-16)
  Length = 8
  Length2 = 5
  Placement = pos=(0,0,-35) rot=(1,0,0;3.14159rad)
  Profile = -> Sketch048
  ReferenceAxis = -> Sketch048 [N_Axis]
  Type = 0
FEATURE [Sketcher::SketchObject] Sketch049
  FullyConstrained = true
  MapMode = 5
  Placement = pos=(0,5,-2.2e-15) rot=(-1,0,0;1.5708rad)
  Support = -> [Pad025]
  sketch-geometry (1):
    g0: Circle CenterX=0 CenterY=0 CenterZ=0 NormalX=0 NormalY=0 NormalZ=1 AngleXU=0 Radius=2.5
  constraints (2):
    c: Coincident(g0,g-1)
    c: Diameter(g0) = 5
FEATURE [PartDesign::Pad] Pad026
  BaseFeature = -> Pad025
  Direction = (0,1,-2e-16)
  Length = 3
  Length2 = 10
  Placement = pos=(0,0,0) rot=(1,0,0;1.5708rad)
  Profile = -> Sketch049
  ReferenceAxis = -> Sketch049 [N_Axis]
  Type = 0
FEATURE [PartDesign::Fillet] Fillet002
  Base = -> Pad026 [Edge51]
  BaseFeature = -> Pad026
  Placement = pos=(0,0,0) rot=(1,0,0;1.5708rad)
  Radius = 2
  SupportTransform = false
  UseAllEdges = false
FEATURE [PartDesign::Fillet] Fillet003
  Base = -> Fillet002 [Edge3]
  BaseFeature = -> Fillet002
  Placement = pos=(0,0,0) rot=(1,0,0;1.5708rad)
  Radius = 7
  SupportTransform = false
  UseAllEdges = false
FEATURE [Sketcher::SketchObject] Sketch050
  ExternalGeometry = -> [Cone003]
  FullyConstrained = true
  MapMode = 5
  Placement = pos=(6e-16,2.5,-35) rot=(-1,0,0;1.5708rad)
  Support = -> [Pocket023]
  expr: Constraints[11] = Sketch048.Constraints[11]
  expr: Constraints[54] = Sketch045.Constraints[43]
  expr: Constraints[55] = Sketch045.Constraints[44]
  sketch-geometry (34):
    g0: LineSegment StartX=-11.75 StartY=-46.75 StartZ=0 EndX=-11.75 EndY=-23.25 EndZ=0
    g1: LineSegment StartX=-11.75 StartY=-23.25 StartZ=0 EndX=11.75 EndY=-23.25 EndZ=0
    g2: LineSegment StartX=11.75 StartY=-23.25 StartZ=0 EndX=11.75 EndY=-46.75 EndZ=0
    g3: LineSegment StartX=11.75 StartY=-46.75 StartZ=0 EndX=-11.75 EndY=-46.75 EndZ=0
    g4: GeomPoint X=-2.4e-15 Y=-35 Z=0
    g5: LineSegment StartX=12 StartY=-37 StartZ=0 EndX=12 EndY=-33 EndZ=0
    g6: LineSegment StartX=12 StartY=-33 StartZ=0 EndX=2 EndY=-33 EndZ=0
    g7: LineSegment StartX=2 StartY=-33 StartZ=0 EndX=2 EndY=-23 EndZ=0
    g8: LineSegment StartX=2 StartY=-23 StartZ=0 EndX=-2 EndY=-23 EndZ=0
    g9: LineSegment StartX=-2 StartY=-23 StartZ=0 EndX=-2 EndY=-33 EndZ=0
    g10: LineSegment StartX=-2 StartY=-33 StartZ=0 EndX=-12 EndY=-33 EndZ=0
    g11: LineSegment StartX=-12 StartY=-33 StartZ=0 EndX=-12 EndY=-37 EndZ=0
    g12: LineSegment StartX=-12 StartY=-37 StartZ=0 EndX=-2 EndY=-37 EndZ=0
    g13: LineSegment StartX=-2 StartY=-37 StartZ=0 EndX=-2 EndY=-47 EndZ=0
    g14: LineSegment StartX=-2 StartY=-47 StartZ=0 EndX=2 EndY=-47 EndZ=0
    g15: LineSegment StartX=2 StartY=-47 StartZ=0 EndX=2 EndY=-37 EndZ=0
    g16: LineSegment StartX=2 StartY=-37 StartZ=0 EndX=12 EndY=-37 EndZ=0
    g17: LineSegment StartX=-2 StartY=-37 StartZ=0 EndX=-2 EndY=-33 EndZ=0
    g18: LineSegment StartX=-2 StartY=-33 StartZ=0 EndX=2 EndY=-33 EndZ=0
    g19: LineSegment StartX=2 StartY=-33 StartZ=0 EndX=2 EndY=-37 EndZ=0
    g20: LineSegment StartX=2 StartY=-37 StartZ=0 EndX=-2 EndY=-37 EndZ=0
    g21: GeomPoint X=0 Y=0 Z=0
    g22: LineSegment StartX=-2 StartY=-23.25 StartZ=0 EndX=2 EndY=-23.25 EndZ=0
    g23: LineSegment StartX=2 StartY=-23.25 StartZ=0 EndX=2 EndY=-33 EndZ=0
    g24: LineSegment StartX=2 StartY=-33 StartZ=0 EndX=11.75 EndY=-33 EndZ=0
    g25: LineSegment StartX=11.75 StartY=-33 StartZ=0 EndX=11.75 EndY=-37 EndZ=0
    g26: LineSegment StartX=11.75 StartY=-37 StartZ=0 EndX=2 EndY=-37 EndZ=0
    g27: LineSegment StartX=2 StartY=-37 StartZ=0 EndX=2 EndY=-46.75 EndZ=0
    g28: LineSegment StartX=2 StartY=-46.75 StartZ=0 EndX=-2 EndY=-46.75 EndZ=0
    g29: LineSegment StartX=-2 StartY=-46.75 StartZ=0 EndX=-2 EndY=-37 EndZ=0
    g30: LineSegment StartX=-2 StartY=-37 StartZ=0 EndX=-11.75 EndY=-37 EndZ=0
    g31: LineSegment StartX=-11.75 StartY=-37 StartZ=0 EndX=-11.75 EndY=-33 EndZ=0
    g32: LineSegment StartX=-11.75 StartY=-33 StartZ=0 EndX=-2 EndY=-33 EndZ=0
    g33: LineSegment StartX=-2 StartY=-33 StartZ=0 EndX=-2 EndY=-23.25 EndZ=0
  constraints (90):
    c: Coincident(g0,g1)
    c: Coincident(g1,g2)
    c: Coincident(g2,g3)
    c: Coincident(g3,g0)
    c: Horizontal(g1)
    c: Horizontal(g3)
    c: Vertical(g0)
    c: Vertical(g2)
    c: Symmetric(g1,g0,g4)
    c: Coincident(g4,g-3)
    c: Equal(g2,g1)
    c: DistanceX(g1,g1) = 23.5
    c: Vertical(g5)
    c: Coincident(g6,g5)
    c: Horizontal(g6)
    c: Coincident(g7,g6)
    c: Vertical(g7)
    c: Coincident(g8,g7)
    c: Horizontal(g8)
    c: Coincident(g9,g8)
    c: Vertical(g9)
    c: Coincident(g10,g9)
    c: Horizontal(g10)
    c: Coincident(g11,g10)
    c: Vertical(g11)
    c: Horizontal(g12)
    c: Coincident(g13,g12)
    c: Vertical(g13)
    c: Horizontal(g14)
    c: Coincident(g15,g14)
    c: Vertical(g15)
    c: Coincident(g16,g15)
    c: Coincident(g16,g5)
    c: Horizontal(g16)
    c: Equal(g5,g8)
    c: Equal(g8,g11)
    c: Equal(g11,g14)
    c: Coincident(g11,g12)
    c: Coincident(g14,g13)
    c: Equal(g16,g12)
    c: Equal(g16,g6)
    c: Equal(g7,g9)
    c: Equal(g10,g15)
    c: Coincident(g17,g18)
    c: Coincident(g18,g19)
    c: Coincident(g19,g20)
    c: Coincident(g20,g17)
    c: Horizontal(g18)
    c: Horizontal(g20)
    c: Vertical(g17)
    c: Vertical(g19)
    c: Coincident(g21,g-1)
    c: Coincident(g18,g6)
    c: Coincident(g12,g17)
    c: DistanceX(g18,g18) = 4
    c: DistanceY(g7,g7) = 10
    c: Equal(g15,g7)
    c: Symmetric(g6,g12,g4)
    c: PointOnObject(g22,g9)
    c: PointOnObject(g22,g1)
    c: Horizontal(g22)
    c: PointOnObject(g22,g7)
    c: Coincident(g23,g22)
    c: Coincident(g23,g6)
    c: Coincident(g24,g23)
    c: PointOnObject(g24,g2)
    c: Horizontal(g24)
    c: Coincident(g25,g24)
    c: PointOnObject(g25,g16)
    c: Vertical(g25)
    c: Coincident(g26,g25)
    c: Coincident(g26,g15)
    c: Coincident(g27,g26)
    c: PointOnObject(g27,g3)
    c: Vertical(g27)
    c: Coincident(g28,g27)
    c: PointOnObject(g28,g13)
    c: Horizontal(g28)
    c: Coincident(g29,g28)
    c: Coincident(g29,g12)
    c: Coincident(g30,g29)
    c: PointOnObject(g30,g0)
    c: Horizontal(g30)
    c: Coincident(g31,g30)
    c: PointOnObject(g31,g10)
    c: Vertical(g31)
    c: Coincident(g32,g31)
    c: Coincident(g32,g9)
    c: Coincident(g33,g32)
    c: Coincident(g33,g22)
FEATURE [PartDesign::Pocket] Pocket024
  BaseFeature = -> Pocket023
  Direction = (-2e-16,-1,2e-16)
  Length = 3
  Length2 = 5
  Placement = pos=(0,0,-35) rot=(1,0,0;3.14159rad)
  Profile = -> Sketch050
  ReferenceAxis = -> Sketch050 [N_Axis]
  Type = 0
FEATURE [PartDesign::Body] Body014  label="HeadInstert001"
  Group = -> [Sketch028,Pad016,Sketch029,Pocket013,Sketch030,Pocket014,Sketch032,Pocket015,Chamfer007,Sketch031,Pocket016,Chamfer008,Sketch036,Pocket019,Chamfer010,Chamfer011,Chamfer012,Cone002,Cone003,Sketch048,Pocket023,Sketch050,Pocket024]
  Origin = -> Origin016
  Tip = -> Pocket024
FEATURE [Sketcher::SketchObject] Sketch051
  FullyConstrained = true
  MapMode = 5
  Placement = pos=(0,0,0) rot=(1,0,0;1.5708rad)
  Support = -> [XZ_Plane026]
  expr: Constraints[1] = <<Properties001>>.Handle_OD - <<Properties001>>.Clearance * 2
  sketch-geometry (1):
    g0: Circle CenterX=0 CenterY=0 CenterZ=0 NormalX=0 NormalY=0 NormalZ=1 AngleXU=0 Radius=10.55
  constraints (2):
    c: Coincident(g0,g-1)
    c: Diameter(g0) = 21.1
FEATURE [PartDesign::Pad] Pad027
  BaseFeature = -> Fillet003
  Direction = (0,-1,2e-16)
  Length = 9
  Length2 = 10
  Placement = pos=(0,0,0) rot=(1,0,0;1.5708rad)
  Profile = -> Sketch051
  ReferenceAxis = -> Sketch051 [N_Axis]
  TaperAngle = -2
  Type = 0
FEATURE [PartDesign::Chamfer] Chamfer013
  Angle = 45
  Base = -> Pad027 [Edge15,Edge19,Edge10,Edge11]
  BaseFeature = -> Pad027
  ChamferType = 0
  FlipDirection = false
  Placement = pos=(0,0,0) rot=(1,0,0;1.5708rad)
  Size = 1
  Size2 = 1
  SupportTransform = false
  UseAllEdges = false
FEATURE [PartDesign::Body] Body025  label="Pusher001"
  Group = -> [Sketch046,Pad024,Sketch047,Pad025,Sketch049,Pad026,Fillet002,Fillet003,Sketch051,Pad027,Chamfer013]
  Origin = -> Origin026
  Placement = pos=(0,62.5,0) rot=(0,0,1;0rad)
  Tip = -> Chamfer013
FEATURE [Sketcher::SketchObject] Sketch052
  FullyConstrained = true
  MapMode = 5
  Placement = pos=(0,0,0) rot=(1,0,0;1.5708rad)
  Support = -> [XZ_Plane027]
  expr: Constraints[1] = <<Properties001>>.Handle_OD - 1
  sketch-geometry (2):
    g0: Circle CenterX=0 CenterY=0 CenterZ=0 NormalX=0 NormalY=0 NormalZ=1 AngleXU=0 Radius=10.25
    g1: Circle CenterX=0 CenterY=0 CenterZ=0 NormalX=0 NormalY=0 NormalZ=1 AngleXU=0 Radius=4
  constraints (4):
    c: Coincident(g0,g-1)
    c: Diameter(g0) = 20.5
    c: Coincident(g1,g0)
    c: Diameter(g1) = 8
FEATURE [PartDesign::Pad] Pad028
  Direction = (0,-1,-2e-16)
  Length = 10
  Length2 = 10
  Placement = pos=(0,0,0) rot=(1,0,0;1.5708rad)
  Profile = -> Sketch052
  ReferenceAxis = -> Sketch052 [N_Axis]
  Type = 0
FEATURE [PartDesign::Draft] Draft001
  Angle = 2
  Base = -> Pad028 [Face1]
  BaseFeature = -> Pad028
  NeutralPlane = -> Pad028 [Face3]
  Placement = pos=(0,0,0) rot=(1,0,0;1.5708rad)
  SupportTransform = false
FEATURE [PartDesign::Body] Body026  label="WirePlug001"
  Group = -> [Sketch052,Pad028,Draft001]
  Origin = -> Origin027
  Placement = pos=(0,-275,0) rot=(0,0,1;0rad)
  Tip = -> Draft001
FEATURE [Sketcher::SketchObject] Sketch053
  FullyConstrained = true
  MapMode = 5
  Placement = pos=(0,0,0) rot=(1,0,0;1.5708rad)
  Support = -> [XZ_Plane017]
  sketch-geometry (5):
    g0: LineSegment StartX=-2.5 StartY=-45 StartZ=0 EndX=-2.5 EndY=45 EndZ=0
    g1: LineSegment StartX=-2.5 StartY=45 StartZ=0 EndX=2.5 EndY=45 EndZ=0
    g2: LineSegment StartX=2.5 StartY=45 StartZ=0 EndX=2.5 EndY=-45 EndZ=0
    g3: LineSegment StartX=2.5 StartY=-45 StartZ=0 EndX=-2.5 EndY=-45 EndZ=0
    g4: GeomPoint X=0 Y=0 Z=0
  constraints (12):
    c: Coincident(g0,g1)
    c: Coincident(g1,g2)
    c: Coincident(g2,g3)
    c: Coincident(g3,g0)
    c: Horizontal(g1)
    c: Horizontal(g3)
    c: Vertical(g0)
    c: Vertical(g2)
    c: Symmetric(g1,g0,g4)
    c: Coincident(g4,g-1)
    c: DistanceX(g1,g1) = 5
    c: DistanceY(g2,g2) = 90
FEATURE [PartDesign::Pocket] Pocket025
  BaseFeature = -> Pocket020
  Direction = (0,1,2e-16)
  Length = 5
  Length2 = 5
  Profile = -> Sketch053
  ReferenceAxis = -> Sketch053 [N_Axis]
  Reversed = true
  Type = 1
FEATURE [PartDesign::Body] Body016  label="PVCHammerHeadShell001"
  Group = -> [Sketch037,Pad018,Sketch038,Pocket020,Sketch053,Pocket025]
  Origin = -> Origin017
  Placement = pos=(0,0,220) rot=(0,0,1;0rad)
  Tip = -> Pocket025
PROVENANCE & LICENSES
A FreeCAD (.FCStd) document from a public repository crawl; recipes are the document's own serialized feature recipes (and, for linked parts, companion documents' recipes).
License: as declared in the source repository (recorded in the dataset sidecar).
